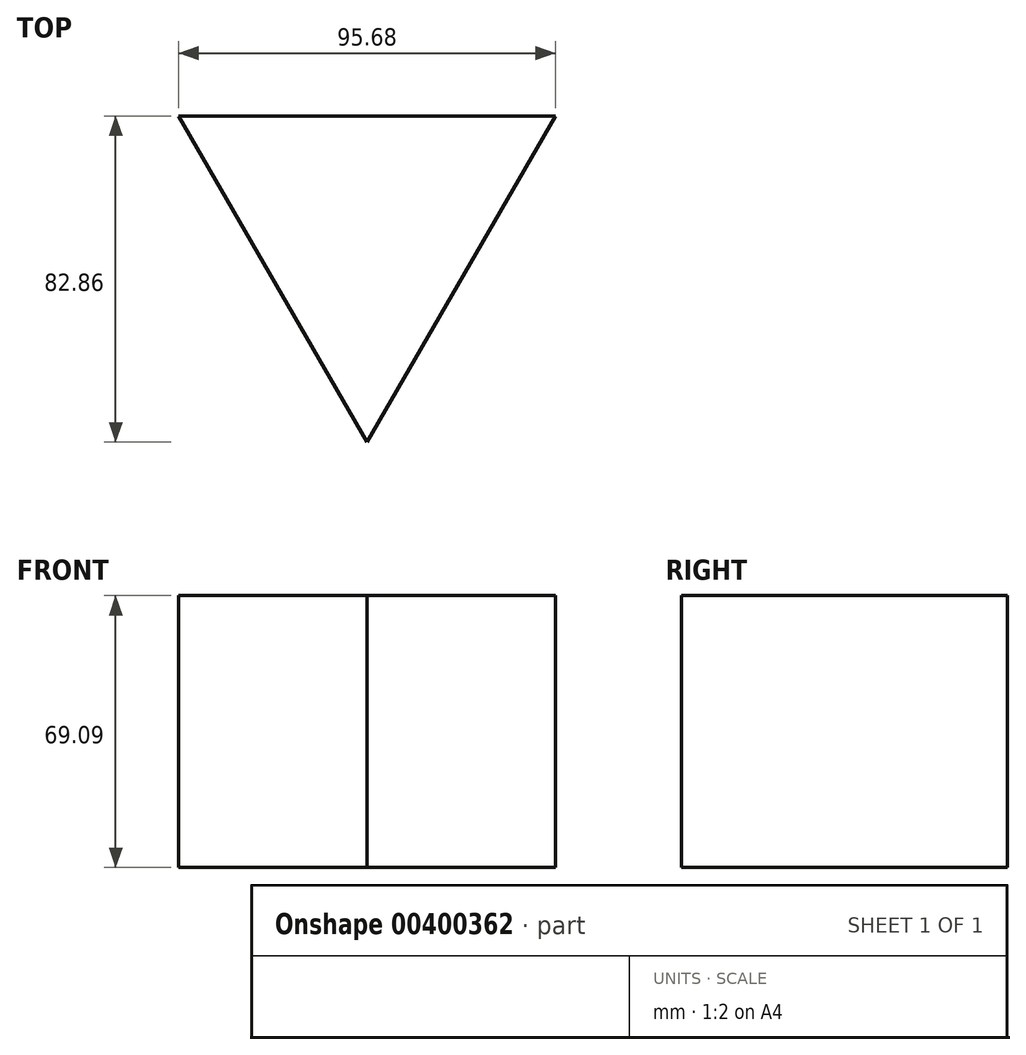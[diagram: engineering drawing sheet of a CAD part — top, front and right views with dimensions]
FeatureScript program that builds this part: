
annotation { "Feature Type Name" : "Feature", "Feature Type Description" : "" }
export const myFeature = defineFeature(function(context is Context, id is Id, definition is map)
    precondition{}
    {
        {
            var Q0;
            Q0=qCreatedBy(makeId("Top.planeOp"),FACE);
            var sketch = newSketch(context, id + "F0", { "sketchPlane" : qUnion([Q0])});
            skText(sketch, "E0", { "text": "Merry Christmas", "fontName": "OpenSans-Bold.ttf"});
            const initialGuessF0  = {"E0": [-0.06237, -0.06786, 1, 0, 0.04037]};
            skSetInitialGuess(sketch, initialGuessF0);
            skSolve(sketch);
        }
        {
            var Q0;
            Q0 = qConstructionFilter(qBodyType(qCreatedBy(id + "F0" ,EDGE), BodyType.WIRE), ConstructionObject.NO);
            extrude(context, id + "F1", {"bodyType" : ToolBodyType.SURFACE, "surfaceEntities" : qUnion([Q0]), "depth" : 25.4 * mm});
        }
        {
            var Q0;
            Q0=qCreatedBy(makeId("Top.planeOp"),FACE);
            var sketch = newSketch(context, id + "F2", { "sketchPlane" : qUnion([Q0])});
            skCircle(sketch, "E1.cCircle", {"center": v(-20.6, 67.47) * mm, "radius": 27.62 * mm, "construction": true});
            skLineSegment(sketch, "E1.0", {"start": v(-68.44, 95.1) * mm, "end": v(27.24, 95.1) * mm});
            skLineSegment(sketch, "E1.1", {"start": v(27.24, 95.1) * mm, "end": v(-20.6, 12.23) * mm});
            skLineSegment(sketch, "E1.2", {"start": v(-20.6, 12.23) * mm, "end": v(-68.44, 95.1) * mm});
            skPoint(sketch, "E1.0.midPoint", {"position": v(-20.6, 95.1) * mm});
            skSolve(sketch);
        }
        {
            var Q0;
            Q0 = qSketchRegion(id + "F2", true);
            extrude(context, id + "F3", {"entities" : qUnion([Q0]), "depth" : 25.4 * mm});
        }
        {
            var Q0;
            Q0=makeQuery(id+"F3.opExtrude","CAP_FACE",FACE,{"disambiguationData":[OSD([sQuery(id+"F2.wireOp",EDGE,"E1.0"),sQuery(id+"F2.wireOp",EDGE,"E1.1"),sQuery(id+"F2.wireOp",EDGE,"E1.2")])],"isStart":false});
            extrude(context, id + "F4", {"entities" : qUnion([Q0]), "operationType" : NewBodyOperationType.ADD, "depth" : 43.69 * mm});
        }
    });
